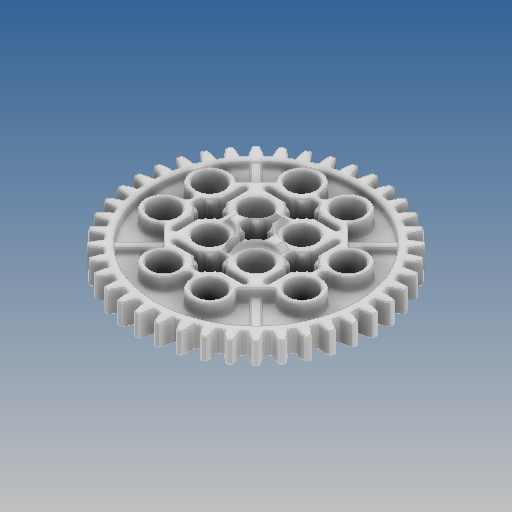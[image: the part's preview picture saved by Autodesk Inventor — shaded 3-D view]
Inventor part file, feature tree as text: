
AUTODESK INVENTOR PART (.ipt)
format: ipt  version: 2020 (Build 240168000, 168)  size: 2,764,800 bytes
history: native  units: mm
features: fillet x1
ambient origin geometry x8: Origin, YZ Plane, XZ Plane, XY Plane, X Axis, Y Axis, Z Axis, Center Point
bodies: Solid1 (feature_tree)
feature tree (1):
  fillet  "Redondeo2"  [1 undecoded]
note: 1 required parameter value undecoded (feature->parameter linkage not recoverable at this tier; creation-order binding heuristic only, values carry confidence <= 0.55)
